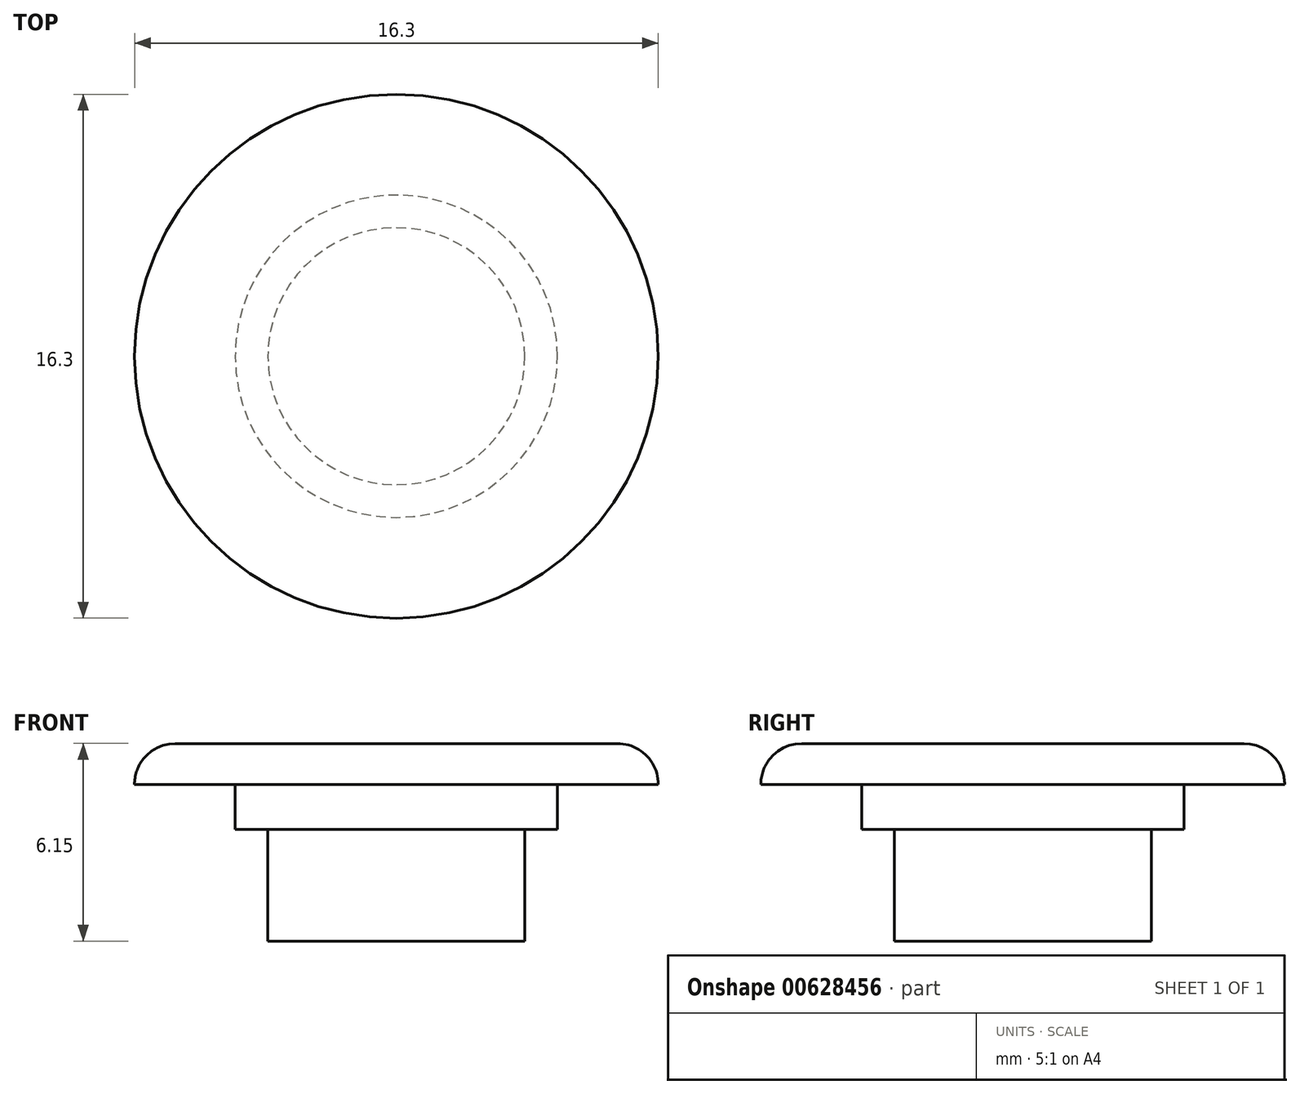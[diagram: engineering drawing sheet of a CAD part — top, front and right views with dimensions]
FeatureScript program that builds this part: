
annotation { "Feature Type Name" : "Feature", "Feature Type Description" : "" }
export const myFeature = defineFeature(function(context is Context, id is Id, definition is map)
    precondition{}
    {
        {
            var Q0;
            Q0=qCreatedBy(makeId("Top.planeOp"),FACE);
            var sketch = newSketch(context, id + "F0", { "sketchPlane" : qUnion([Q0])});
            skCircle(sketch, "E0", {"center": v(0, 0) * mm, "radius": 4 * mm});
            skCircle(sketch, "E1.0", {"center": v(0, 0) * mm, "radius": 5.02 * mm});
            skCircle(sketch, "E2.0", {"center": v(0, 0) * mm, "radius": 8.2 * mm});
            skSolve(sketch);
        }
        {
            var Q0;
            Q0=makeQuery(id+"F0.imprint","IMPRINT",FACE,{"disambiguationData":[TD([[makeQuery(id+"F0.imprint","IMPRINT",EDGE,{"derivedFrom":sQuery(id+"F0.wireOp",EDGE,"E0")}),1.0]])]});
            extrude(context, id + "F1", {"entities" : qUnion([Q0]), "oppositeDirection" : true, "depth" : 3.48 * mm, "offsetDistance" : 25.4 * mm});
        }
        {
            var Q0;
            Q0=makeQuery(id+"F0.imprint","IMPRINT",FACE,{"disambiguationData":[TD([[makeQuery(id+"F0.imprint","IMPRINT",EDGE,{"derivedFrom":sQuery(id+"F0.wireOp",EDGE,"E0")}),-1.0]])]});
            var Q1;
            Q1=makeQuery(id+"F0.imprint","IMPRINT",FACE,{"disambiguationData":[TD([[makeQuery(id+"F0.imprint","IMPRINT",EDGE,{"derivedFrom":sQuery(id+"F0.wireOp",EDGE,"E0")}),1.0]])]});
            extrude(context, id + "F2", {"entities" : qUnion([Q0, Q1]), "operationType" : NewBodyOperationType.ADD, "depth" : 1.4 * mm, "offsetDistance" : 25.4 * mm});
        }
        {
            var Q0;
            Q0=makeQuery(id+"F2.opExtrude","CAP_FACE",FACE,{"disambiguationData":[OSD([sQuery(id+"F0.wireOp",EDGE,"E1.0")])],"isStart":false});
            var sketch = newSketch(context, id + "F3", { "sketchPlane" : qUnion([Q0])});
            skCircle(sketch, "E3.0", {"center": v(0, 0) * mm, "radius": 8.15 * mm});
            skSolve(sketch);
        }
        {
            var Q0;
            Q0=makeQuery(id+"F3.imprint","IMPRINT",FACE,{"disambiguationData":[TD([[makeQuery(id+"F3.imprint","IMPRINT",EDGE,{"derivedFrom":sQuery(id+"F3.wireOp",EDGE,"E3.0")}),1.0]])]});
            var Q1;
            Q1=makeQuery(id+"F3.imprint","IMPRINT",FACE,{"disambiguationData":[TD([[makeQuery(id+"F3.imprint","IMPRINT",EDGE,{"derivedFrom":makeQuery(id+"F2.opExtrude","CAP_EDGE",EDGE,{"disambiguationData":[OSD([sQuery(id+"F0.wireOp",EDGE,"E1.0")])],"isStart":false})}),1.0]])]});
            extrude(context, id + "F4", {"entities" : qUnion([Q0, Q1]), "operationType" : NewBodyOperationType.ADD, "depth" : 1.27 * mm, "offsetDistance" : 25.4 * mm});
        }
        {
            var Q0;
            Q0=makeQuery(id+"F4.opExtrude","CAP_EDGE",EDGE,{"disambiguationData":[OSD([sQuery(id+"F3.wireOp",EDGE,"E3.0")])],"isStart":false});
            fillet(context, id + "F5", {"entities" : qUnion([Q0]), "radius" : 1.27 * mm, "tangentPropagation" : true, "allowEdgeOverflow" : false});
        }
    });
